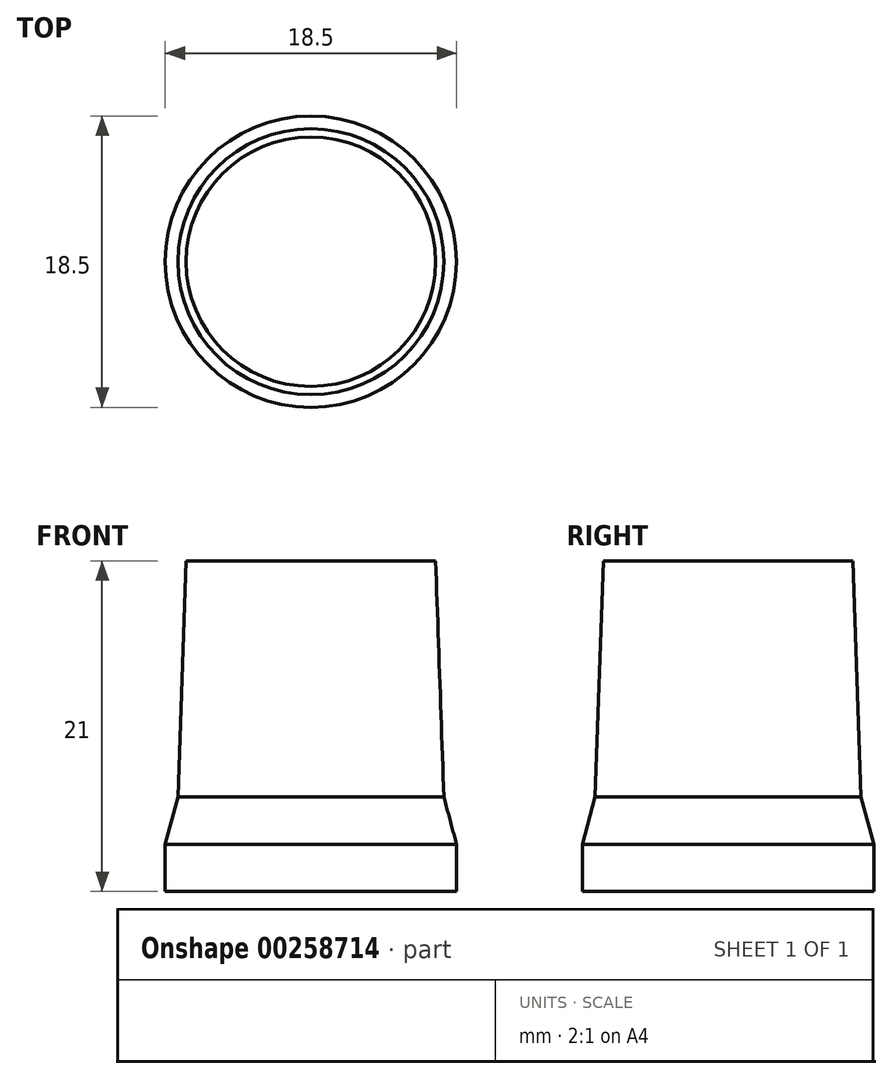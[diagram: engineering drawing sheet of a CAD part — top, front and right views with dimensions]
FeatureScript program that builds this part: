
annotation { "Feature Type Name" : "Feature", "Feature Type Description" : "" }
export const myFeature = defineFeature(function(context is Context, id is Id, definition is map)
    precondition{}
    {
        {
            var Q0;
            Q0=qCreatedBy(makeId("Top.planeOp"),FACE);
            var sketch = newSketch(context, id + "F0", { "sketchPlane" : qUnion([Q0])});
            skCircle(sketch, "E0", {"center": v(0, 0) * mm, "radius": 9.25 * mm});
            skSolve(sketch);
        }
        {
            var Q0;
            Q0 = qSketchRegion(id + "F0", true);
            extrude(context, id + "F1", {"entities" : qUnion([Q0]), "depth" : 3 * mm});
        }
        {
            var Q0;
            Q0=makeQuery(id+"F1.opExtrude","CAP_FACE",FACE,{"disambiguationData":[OSD([sQuery(id+"F0.wireOp",EDGE,"E0")])],"isStart":false});
            extrude(context, id + "F2", {"entities" : qUnion([Q0]), "operationType" : NewBodyOperationType.ADD, "depth" : 3 * mm, "hasDraft" : true, "draftAngle" : 15 * degree, "draftPullDirection" : true});
        }
        {
            var Q0;
            Q0=makeQuery(id+"F2.opExtrude","CAP_FACE",FACE,{"disambiguationData":[OSD([sQuery(id+"F0.wireOp",EDGE,"E0")])],"isStart":false});
            extrude(context, id + "F3", {"entities" : qUnion([Q0]), "operationType" : NewBodyOperationType.ADD, "depth" : 15 * mm, "hasDraft" : true, "draftAngle" : 2 * degree, "draftPullDirection" : true});
        }
    });
